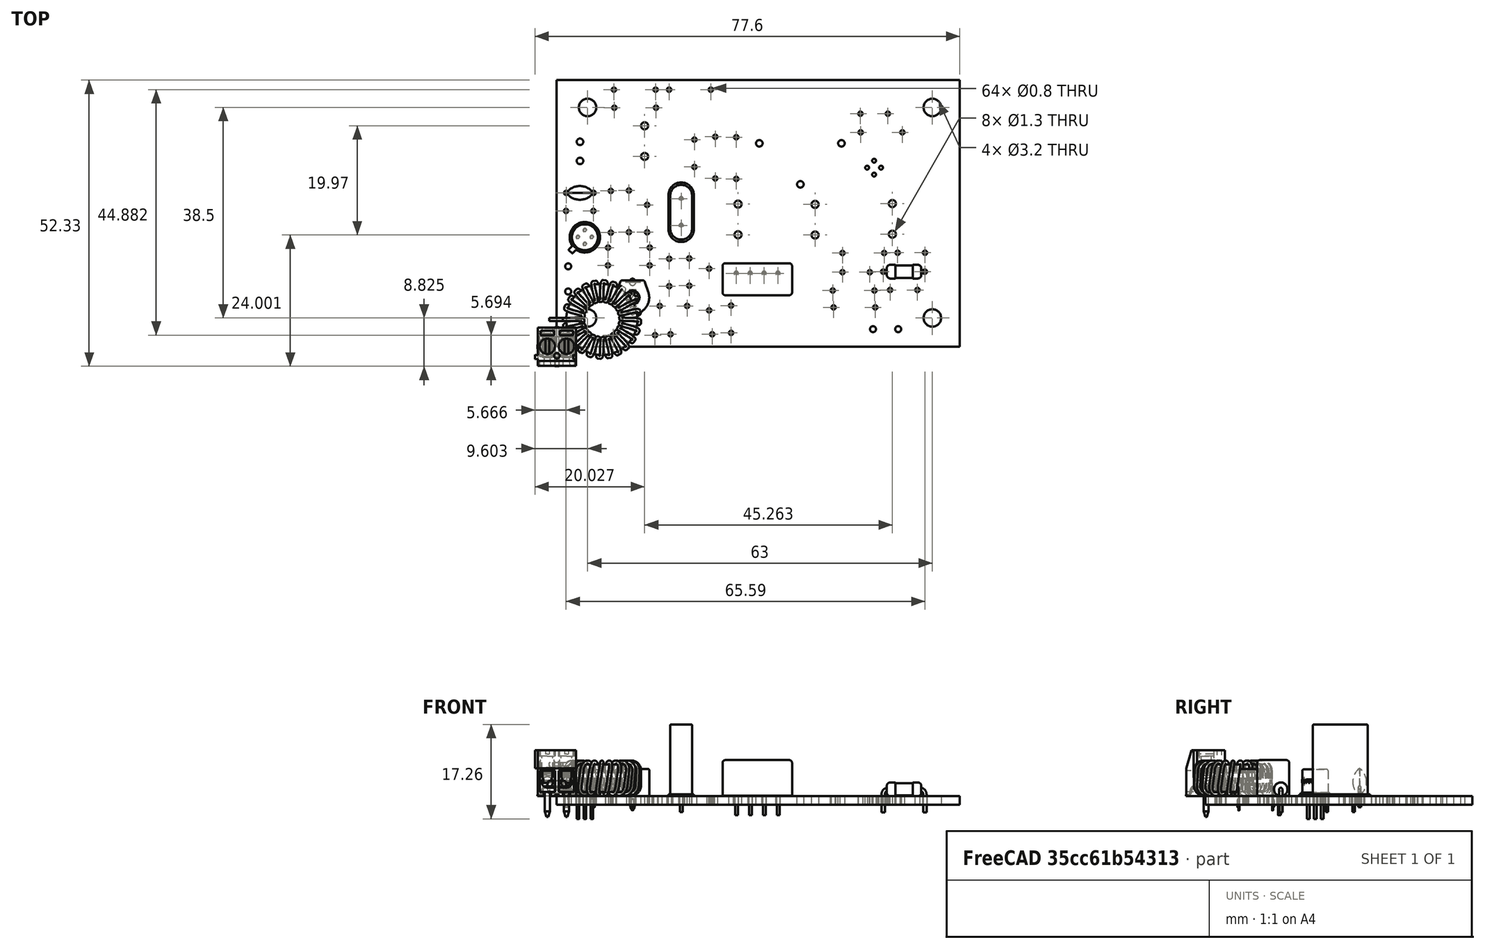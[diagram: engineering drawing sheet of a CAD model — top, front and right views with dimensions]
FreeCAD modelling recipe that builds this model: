
FCSTD DOCUMENT  (FreeCAD 0.19R24267 +148 (Git))
Label: 2ndmixer-2ndlo
License: All rights reserved
LicenseURL: http://en.wikipedia.org/wiki/All_rights_reserved
objects: App::Link×41, Part::Feature×33, App::Part×8, PartDesign::CoordinateSystem×1, Sketcher::SketchObject×1
note: 35 computed .brp shape members not serialized (recipe doc carries the construction recipe); baked Part::Feature solids carry a one-line shape summary decoded from their .brp

FEATURE [PartDesign::CoordinateSystem] Local_CS_b4da
  AttacherType = Attacher::AttachEngine3D
FEATURE [Part::Feature] Pcb_b4da
  Placement = pos=(-101.397,124.765,0) rot=(0,0,1;0rad)
  shape: bbox 73.68 x 48.77 x 1.6 mm, 101 faces (baked)
FEATURE [Sketcher::SketchObject] PCB_Sketch_b4da
  FullyConstrained = false
  sketch-geometry (4):
    g0: LineSegment StartX=-0.077005 StartY=0 StartZ=0 EndX=73.6032 EndY=0 EndZ=0
    g1: LineSegment StartX=73.6032 StartY=48.768 StartZ=0 EndX=-0.077005 EndY=48.768 EndZ=0
    g2: LineSegment StartX=73.6032 StartY=0 StartZ=0 EndX=73.6032 EndY=48.768 EndZ=0
    g3: LineSegment StartX=-0.077005 StartY=48.768 StartZ=0 EndX=-0.077005 EndY=0 EndZ=0
  constraints (4):
    c: Coincident(g0,g3)
    c: Coincident(g1,g3)
    c: Coincident(g0,g2)
    c: Coincident(g1,g2)
FEATURE [Part::Feature] Shape  label="R217_R_Axial_DIN0207_L63mm_D25mm_P762mm_Horizontal_89c8d03f2e72"
  Placement = pos=(59.6138,13.7414,0) rot=(0,0,1;0rad)
  shape: bbox 8.418 x 2.706 x 5.603 mm, 15 faces (baked)
FEATURE [Part::Feature] Shape001  label="C203_C_Disc_D50mm_W25mm_P500mm_089fd93012b2"
  Placement = pos=(6.691,28.1432,0) rot=(0,0,1;3.14159rad)
  shape: bbox 5.5 x 2.5 x 7.1 mm, 10 faces (baked)
FEATURE [App::Link] R217_R_Axial_DIN0207_L63mm_D25mm_P762mm_Horizontal_89c8d03f2e72_ln_  label="R213_R_Axial_DIN0207_L63mm_D25mm_P762mm_Horizontal_cce2eee8a25c"
  LinkPlacement = pos=(55.499,39.2176,0) rot=(0,0,1;0rad)
  LinkedObject = -> Shape
  Placement = pos=(55.499,39.2176,0) rot=(0,0,1;0rad)
FEATURE [App::Link] C203_C_Disc_D50mm_W25mm_P500mm_089fd93012b2_ln_  label="C205_C_Disc_D50mm_W25mm_P500mm_a9d93c2b414c"
  LinkPlacement = pos=(20.5232,16.089,0) rot=(0,0,-1;1.5708rad)
  LinkedObject = -> Shape001
  Placement = pos=(20.5232,16.089,0) rot=(0,0,-1;1.5708rad)
FEATURE [Part::Feature] Shape002  label="C206_Trimmer Cap - Brown_62b893ec28ea"
  Placement = pos=(13.8176,9.011,0) rot=(0,0,1;3.14159rad)
  shape: bbox 6.618 x 6.858 x 7.625 mm, 264 faces (baked)
FEATURE [App::Link] C206_Trimmer_Cap___Brown_62b893ec28ea_ln_  label="C206_Trimmer Cap - Brown_62b893ec28ea[2]"
  LinkPlacement = pos=(13.8176,11.811,0) rot=(0,0,-1;1.5708rad)
  LinkedObject = -> Shape002
  Placement = pos=(13.8176,11.811,0) rot=(0,0,-1;1.5708rad)
FEATURE [App::Link] R217_R_Axial_DIN0207_L63mm_D25mm_P762mm_Horizontal_89c8d03f2e72_ln_001  label="R211_R_Axial_DIN0207_L63mm_D25mm_P762mm_Horizontal_9d0fcc912394"
  LinkPlacement = pos=(32.766,38.3286,0) rot=(0,0,-1;1.5708rad)
  LinkedObject = -> Shape
  Placement = pos=(32.766,38.3286,0) rot=(0,0,-1;1.5708rad)
FEATURE [App::Link] R217_R_Axial_DIN0207_L63mm_D25mm_P762mm_Horizontal_89c8d03f2e72_ln_002  label="R216_R_Axial_DIN0207_L63mm_D25mm_P762mm_Horizontal_da9762c644fc"
  LinkPlacement = pos=(58.166,7.2136,0) rot=(0,0,1;3.14159rad)
  LinkedObject = -> Shape
  Placement = pos=(58.166,7.2136,0) rot=(0,0,1;3.14159rad)
FEATURE [Part::Feature] Part__Feature  label="SOLID"
  Placement = pos=(0,0,4.2) rot=(0,0,1;0rad)
  shape: bbox 8 x 7 x 8.4 mm, 72 faces (baked)
FEATURE [Part::Feature] Part__Feature001  label="SOLID001"
  Placement = pos=(0,0,4.2) rot=(0,0,1;0rad)
  shape: bbox 2.75 x 3.75 x 8.15 mm, 17 faces (baked)
FEATURE [Part::Feature] Part__Feature002  label="SOLID002"
  Placement = pos=(0,0,4.2) rot=(0,0,1;0rad)
  shape: bbox 2.75 x 3.75 x 8.15 mm, 17 faces (baked)
FEATURE [Part::Feature] Part__Feature003  label="SOLID003"
  Placement = pos=(0,0,4.2) rot=(0,0,1;0rad)
  shape: bbox 2.9 x 4.5 x 2.65 mm, 46 faces (baked)
FEATURE [Part::Feature] Part__Feature004  label="SOLID004"
  Placement = pos=(0,0,4.2) rot=(0,0,1;0rad)
  shape: bbox 2.9 x 4.5 x 2.65 mm, 46 faces (baked)
FEATURE [Part::Feature] Part__Feature005  label="SOLID005"
  Placement = pos=(0,0,4.2) rot=(0,0,1;0rad)
  shape: bbox 3.139 x 3.139 x 4.6 mm, 17 faces (baked)
FEATURE [Part::Feature] Part__Feature006  label="SOLID006"
  Placement = pos=(0,0,4.2) rot=(0,0,1;0rad)
  shape: bbox 3.139 x 3.139 x 4.6 mm, 17 faces (baked)
FEATURE [App::Part] _91103110002_1  label="J202_691103110002_1_e432b8dc621c"
  Group = -> [Part__Feature,Part__Feature001,Part__Feature002,Part__Feature003,Part__Feature004,Part__Feature005,Part__Feature006]
  Origin = -> Origin008
  Placement = pos=(4.2164,35.7378,0) rot=(0,0,1;1.5708rad)
FEATURE [App::Link] J202_691103110002_1_e432b8dc621c_ln_  label="J202_691103110002_1_e432b8dc621c[2]"
  LinkPlacement = pos=(4.2164,35.7378,0) rot=(0,0,1;1.5708rad)
  LinkedObject = -> _91103110002_1
  Placement = pos=(4.2164,35.7378,0) rot=(0,0,1;1.5708rad)
FEATURE [App::Link] R217_R_Axial_DIN0207_L63mm_D25mm_P762mm_Horizontal_89c8d03f2e72_ln_003  label="R206_R_Axial_DIN0207_L63mm_D25mm_P762mm_Horizontal_b9c1ee328a49"
  LinkPlacement = pos=(17.9324,2.1336,0) rot=(0,0,1;3.14159rad)
  LinkedObject = -> Shape
  Placement = pos=(17.9324,2.1336,0) rot=(0,0,1;3.14159rad)
FEATURE [App::Link] C203_C_Disc_D50mm_W25mm_P500mm_089fd93012b2_ln_001  label="C212_C_Disc_D50mm_W25mm_P500mm_bde68aed2039"
  LinkPlacement = pos=(62.2554,17.1958,0) rot=(0,0,1;0rad)
  LinkedObject = -> Shape001
  Placement = pos=(62.2554,17.1958,0) rot=(0,0,1;0rad)
FEATURE [App::Link] C203_C_Disc_D50mm_W25mm_P500mm_089fd93012b2_ln_002  label="C209_C_Disc_D50mm_W25mm_P500mm_380680a835a4"
  LinkPlacement = pos=(31.8262,2.54,0) rot=(0,0,1;1.5708rad)
  LinkedObject = -> Shape001
  Placement = pos=(31.8262,2.54,0) rot=(0,0,1;1.5708rad)
FEATURE [App::Link] R217_R_Axial_DIN0207_L63mm_D25mm_P762mm_Horizontal_89c8d03f2e72_ln_004  label="R205_R_Axial_DIN0207_L63mm_D25mm_P762mm_Horizontal_e8206ead489c"
  LinkPlacement = pos=(9.3218,14.8844,0) rot=(0,0,1;0rad)
  LinkedObject = -> Shape
  Placement = pos=(9.3218,14.8844,0) rot=(0,0,1;0rad)
FEATURE [App::Link] R217_R_Axial_DIN0207_L63mm_D25mm_P762mm_Horizontal_89c8d03f2e72_ln_005  label="R203_R_Axial_DIN0207_L63mm_D25mm_P762mm_Horizontal_4a083b21630a"
  LinkPlacement = pos=(13.1572,28.575,0) rot=(0,0,-1;1.5708rad)
  LinkedObject = -> Shape
  Placement = pos=(13.1572,28.575,0) rot=(0,0,-1;1.5708rad)
FEATURE [App::Link] R217_R_Axial_DIN0207_L63mm_D25mm_P762mm_Horizontal_89c8d03f2e72_ln_006  label="R214_R_Axial_DIN0207_L63mm_D25mm_P762mm_Horizontal_72fafbfdd86e"
  LinkPlacement = pos=(58.0136,10.287,0) rot=(0,0,1;3.14159rad)
  LinkedObject = -> Shape
  Placement = pos=(58.0136,10.287,0) rot=(0,0,1;3.14159rad)
FEATURE [App::Link] R217_R_Axial_DIN0207_L63mm_D25mm_P762mm_Horizontal_89c8d03f2e72_ln_007  label="R215_R_Axial_DIN0207_L63mm_D25mm_P762mm_Horizontal_28d317cf12d8"
  LinkPlacement = pos=(20.4978,47.0154,0) rot=(0,0,1;0rad)
  LinkedObject = -> Shape
  Placement = pos=(20.4978,47.0154,0) rot=(0,0,1;0rad)
FEATURE [App::Link] R217_R_Axial_DIN0207_L63mm_D25mm_P762mm_Horizontal_89c8d03f2e72_ln_008  label="R207_R_Axial_DIN0207_L63mm_D25mm_P762mm_Horizontal_df0c2504f956"
  LinkPlacement = pos=(28.3718,2.286,0) rot=(0,0,1;3.14159rad)
  LinkedObject = -> Shape
  Placement = pos=(28.3718,2.286,0) rot=(0,0,1;3.14159rad)
FEATURE [Part::Feature] Part__Feature007  label="part"
  shape: bbox 0.1473 x 0.1473 x 0.003 mm, 3 faces (baked)
FEATURE [Part::Feature] Part__Feature008  label="part001"
  shape: bbox 3.686 x 3.686 x 2.289 mm, 14 faces (baked)
FEATURE [Part::Feature] Part__Feature009  label="part002"
  shape: bbox 1.717 x 0.764 x 1.78 mm, 14 faces (baked)
FEATURE [Part::Feature] Part__Feature010  label="part003"
  shape: bbox 0.764 x 1.717 x 1.78 mm, 14 faces (baked)
FEATURE [Part::Feature] Part__Feature011  label="part004"
  shape: bbox 1.717 x 0.764 x 1.78 mm, 14 faces (baked)
FEATURE [Part::Feature] Part__Feature012  label="part005"
  shape: bbox 0.764 x 1.717 x 1.78 mm, 14 faces (baked)
FEATURE [App::Part] part  label="U201_part006_e06496575535"
  Group = -> [Part__Feature007,Part__Feature008,Part__Feature009,Part__Feature010,Part__Feature011,Part__Feature012]
  Origin = -> Origin009
  Placement = pos=(41.0337,4.8133,0) rot=(0,0,1;0rad)
FEATURE [Part::Feature] Part__Feature013  label="T37-6 IND"
  Placement = pos=(0,-2.7,-0.5) rot=(1,0,0;1.5708rad)
  shape: bbox 10.32 x 3.252 x 10.32 mm, 8 faces, 0 solids (baked)
FEATURE [Part::Feature] Part__Feature014  label="T37-6 IND001"
  Placement = pos=(0,-2.7,-0.5) rot=(1,0,0;1.5708rad)
  shape: bbox 10.51 x 3.773 x 9.618 mm, 81 faces, 0 solids (baked)
FEATURE [Part::Feature] Part__Feature015  label="T37-6 IND002"
  Placement = pos=(0,-2.7,-0.5) rot=(1,0,0;1.5708rad)
  shape: bbox 2.23 x 4.584 x 1.894 mm, 1 faces, 0 solids (baked)
FEATURE [Part::Feature] Part__Feature016  label="T37-6 IND003"
  Placement = pos=(0,-2.7,-0.5) rot=(1,0,0;1.5708rad)
  shape: bbox 1.873 x 4.219 x 1.831 mm, 1 faces, 0 solids (baked)
FEATURE [App::Part] T37_6_IND004  label="L202_T37-6 IND004_038137819fb8"
  Group = -> [Part__Feature013,Part__Feature014,Part__Feature015,Part__Feature016]
  Origin = -> Origin010
  Placement = pos=(61.2902,26.1874,0) rot=(0,0,1;0rad)
FEATURE [App::Link] L202_T37_6_IND004_038137819fb8_ln_  label="L202_T37-6 IND004_038137819fb8[2]"
  LinkPlacement = pos=(61.2902,26.1874,0) rot=(0,0,1;0rad)
  LinkedObject = -> T37_6_IND004
  Placement = pos=(61.2902,26.1874,0) rot=(0,0,1;0rad)
FEATURE [App::Link] R217_R_Axial_DIN0207_L63mm_D25mm_P762mm_Horizontal_89c8d03f2e72_ln_009  label="R201_R_Axial_DIN0207_L63mm_D25mm_P762mm_Horizontal_8da1f1e041d0"
  LinkPlacement = pos=(9.8552,28.4988,0) rot=(0,0,-1;1.5708rad)
  LinkedObject = -> Shape
  Placement = pos=(9.8552,28.4988,0) rot=(0,0,-1;1.5708rad)
FEATURE [App::Link] C203_C_Disc_D50mm_W25mm_P500mm_089fd93012b2_ln_003  label="C208_C_Disc_D50mm_W25mm_P500mm_939057481a42"
  LinkPlacement = pos=(23.7852,7.4676,0) rot=(0,0,1;3.14159rad)
  LinkedObject = -> Shape001
  Placement = pos=(23.7852,7.4676,0) rot=(0,0,1;3.14159rad)
FEATURE [App::Link] C203_C_Disc_D50mm_W25mm_P500mm_089fd93012b2_ln_004  label="C201_C_Disc_D50mm_W25mm_P500mm_a150a43b3eb5"
  LinkPlacement = pos=(6.6656,24.8412,0) rot=(0,0,1;3.14159rad)
  LinkedObject = -> Shape001
  Placement = pos=(6.6656,24.8412,0) rot=(0,0,1;3.14159rad)
FEATURE [Part::Feature] Shape003  label="U202_Body002_17581df04f6c"
  Placement = pos=(32.766,13.4336,0) rot=(0,0,1;0rad)
  shape: bbox 12.7 x 5.84 x 10.04 mm, 26 faces (baked)
FEATURE [App::Link] U202_Body002_17581df04f6c_ln_  label="U202_Body002_17581df04f6c[2]"
  LinkPlacement = pos=(32.766,13.4336,0) rot=(0,0,1;0rad)
  LinkedObject = -> Shape003
  Placement = pos=(32.766,13.4336,0) rot=(0,0,1;0rad)
FEATURE [Part::Feature] Shape004  label="Q201_2N3331_31b1c5c0a01c"
  Placement = pos=(5.1108,20.0299,0) rot=(0,0,1;1.5708rad)
  shape: bbox 9.871 x 5.726 x 9.026 mm, 166 faces (baked)
FEATURE [App::Link] Q201_2N3331_31b1c5c0a01c_ln_  label="Q201_2N3331_31b1c5c0a01c[2]"
  LinkPlacement = pos=(5.1108,20.0299,0) rot=(0,0,1;1.5708rad)
  LinkedObject = -> Shape004
  Placement = pos=(5.1108,20.0299,0) rot=(0,0,1;1.5708rad)
FEATURE [App::Link] R217_R_Axial_DIN0207_L63mm_D25mm_P762mm_Horizontal_89c8d03f2e72_ln_010  label="R208_R_Axial_DIN0207_L63mm_D25mm_P762mm_Horizontal_da094b9ea651"
  LinkPlacement = pos=(27.813,6.6548,0) rot=(0,0,1;1.5708rad)
  LinkedObject = -> Shape
  Placement = pos=(27.813,6.6548,0) rot=(0,0,1;1.5708rad)
FEATURE [App::Link] C203_C_Disc_D50mm_W25mm_P500mm_089fd93012b2_ln_005  label="C207_C_Disc_D50mm_W25mm_P500mm_b71f5eab2dcd"
  LinkPlacement = pos=(24.1808,16.1652,0) rot=(0,0,-1;1.5708rad)
  LinkedObject = -> Shape001
  Placement = pos=(24.1808,16.1652,0) rot=(0,0,-1;1.5708rad)
FEATURE [App::Link] C203_C_Disc_D50mm_W25mm_P500mm_089fd93012b2_ln_006  label="C214_C_Disc_D50mm_W25mm_P500mm_07d36dee86ff"
  LinkPlacement = pos=(65.873,10.3886,0) rot=(0,0,1;3.14159rad)
  LinkedObject = -> Shape001
  Placement = pos=(65.873,10.3886,0) rot=(0,0,1;3.14159rad)
FEATURE [App::Link] C203_C_Disc_D50mm_W25mm_P500mm_089fd93012b2_ln_007  label="C213_C_Disc_D50mm_W25mm_P500mm_87d95f91cfc0"
  LinkPlacement = pos=(60.4628,42.6212,0) rot=(0,0,1;3.14159rad)
  LinkedObject = -> Shape001
  Placement = pos=(60.4628,42.6212,0) rot=(0,0,1;3.14159rad)
FEATURE [App::Link] R217_R_Axial_DIN0207_L63mm_D25mm_P762mm_Horizontal_89c8d03f2e72_ln_011  label="R202_R_Axial_DIN0207_L63mm_D25mm_P762mm_Horizontal_28998dc9bd10"
  LinkPlacement = pos=(9.3472,18.1356,0) rot=(0,0,1;0rad)
  LinkedObject = -> Shape
  Placement = pos=(9.3472,18.1356,0) rot=(0,0,1;0rad)
FEATURE [App::Link] R217_R_Axial_DIN0207_L63mm_D25mm_P762mm_Horizontal_89c8d03f2e72_ln_012  label="R210_R_Axial_DIN0207_L63mm_D25mm_P762mm_Horizontal_304976f6f522"
  LinkPlacement = pos=(10.414,47.0154,0) rot=(0,0,1;0rad)
  LinkedObject = -> Shape
  Placement = pos=(10.414,47.0154,0) rot=(0,0,1;0rad)
FEATURE [App::Link] C203_C_Disc_D50mm_W25mm_P500mm_089fd93012b2_ln_008  label="C211_C_Disc_D50mm_W25mm_P500mm_938715400f50"
  LinkPlacement = pos=(57.1754,13.6398,0) rot=(0,0,1;3.14159rad)
  LinkedObject = -> Shape001
  Placement = pos=(57.1754,13.6398,0) rot=(0,0,1;3.14159rad)
FEATURE [App::Link] R217_R_Axial_DIN0207_L63mm_D25mm_P762mm_Horizontal_89c8d03f2e72_ln_013  label="R212_R_Axial_DIN0207_L63mm_D25mm_P762mm_Horizontal_e728fa45b572"
  LinkPlacement = pos=(52.1716,17.145,0) rot=(0,0,1;0rad)
  LinkedObject = -> Shape
  Placement = pos=(52.1716,17.145,0) rot=(0,0,1;0rad)
FEATURE [Part::Feature] Shape005  label="Y201_Crystal_HC49-U_Vertical_7b5f2de54ed7"
  Placement = pos=(22.7076,27.051,0) rot=(0,0,-1;1.5708rad)
  shape: bbox 4.65 x 10.9 x 16 mm, 26 faces (baked)
FEATURE [App::Link] C203_C_Disc_D50mm_W25mm_P500mm_089fd93012b2_ln_009  label="C210_C_Disc_D50mm_W25mm_P500mm_7240768806ec"
  LinkPlacement = pos=(25.1206,37.8822,0) rot=(0,0,-1;1.5708rad)
  LinkedObject = -> Shape001
  Placement = pos=(25.1206,37.8822,0) rot=(0,0,-1;1.5708rad)
FEATURE [App::Link] R217_R_Axial_DIN0207_L63mm_D25mm_P762mm_Horizontal_89c8d03f2e72_ln_014  label="R209_R_Axial_DIN0207_L63mm_D25mm_P762mm_Horizontal_1e766996dd06"
  LinkPlacement = pos=(28.9306,38.4048,0) rot=(0,0,-1;1.5708rad)
  LinkedObject = -> Shape
  Placement = pos=(28.9306,38.4048,0) rot=(0,0,-1;1.5708rad)
FEATURE [App::Link] Q201_2N3331_31b1c5c0a01c_ln_001  label="Q202_2N3331_59fc3119a439"
  LinkPlacement = pos=(57.9521,32.7606,0) rot=(0,0,1;0rad)
  LinkedObject = -> Shape004
  Placement = pos=(57.9521,32.7606,0) rot=(0,0,1;0rad)
FEATURE [App::Link] Q201_2N3331_31b1c5c0a01c_ln_002  label="Q202_2N3331_59fc3119a439[2]"
  LinkPlacement = pos=(57.9521,32.7606,0) rot=(0,0,1;0rad)
  LinkedObject = -> Shape004
  Placement = pos=(57.9521,32.7606,0) rot=(0,0,1;0rad)
FEATURE [App::Link] L202_T37_6_IND004_038137819fb8_ln_001  label="L204_T37-6 IND004_7a62be4f95a9"
  LinkPlacement = pos=(47.1678,26.041,0) rot=(0,0,1;0rad)
  LinkedObject = -> T37_6_IND004
  Placement = pos=(47.1678,26.041,0) rot=(0,0,1;0rad)
FEATURE [App::Link] L202_T37_6_IND004_038137819fb8_ln_002  label="L204_T37-6 IND004_7a62be4f95a9[2]"
  LinkPlacement = pos=(47.1678,26.041,0) rot=(0,0,1;0rad)
  LinkedObject = -> T37_6_IND004
  Placement = pos=(47.1678,26.041,0) rot=(0,0,1;0rad)
FEATURE [App::Link] L202_T37_6_IND004_038137819fb8_ln_003  label="L203_T37-6 IND004_40d8894a6aec"
  LinkPlacement = pos=(33.0962,26.0918,0) rot=(0,0,1;0rad)
  LinkedObject = -> T37_6_IND004
  Placement = pos=(33.0962,26.0918,0) rot=(0,0,1;0rad)
FEATURE [App::Link] L202_T37_6_IND004_038137819fb8_ln_004  label="L203_T37-6 IND004_40d8894a6aec[2]"
  LinkPlacement = pos=(33.0962,26.0918,0) rot=(0,0,1;0rad)
  LinkedObject = -> T37_6_IND004
  Placement = pos=(33.0962,26.0918,0) rot=(0,0,1;0rad)
FEATURE [Part::Feature] Part__Feature017  label="L_Tor_13x8x5_3a_cp"
  shape: bbox 14.07 x 14.07 x 5 mm, 8 faces (baked)
FEATURE [Part::Feature] Part__Feature018  label="L_Tor_13x8x5_3a_cp001"
  shape: bbox 16.93 x 14.67 x 6.694 mm, 203 faces (baked)
FEATURE [App::Part] L_Tor_13x8x5_3a_cp  label="T201_L_Tor_13x8x5_3a_cp002_c358b2f006f9"
  Group = -> [Part__Feature017,Part__Feature018]
  Origin = -> Origin011
  Placement = pos=(36.9824,32.211,0) rot=(0,0,1;0rad)
FEATURE [App::Link] T201_L_Tor_13x8x5_3a_cp002_c358b2f006f9_ln_  label="T201_L_Tor_13x8x5_3a_cp002_c358b2f006f9[2]"
  LinkPlacement = pos=(36.9824,32.211,0) rot=(0,0,1;0rad)
  LinkedObject = -> L_Tor_13x8x5_3a_cp
  Placement = pos=(36.9824,32.211,0) rot=(0,0,1;0rad)
FEATURE [App::Link] R217_R_Axial_DIN0207_L63mm_D25mm_P762mm_Horizontal_89c8d03f2e72_ln_015  label="R204_R_Axial_DIN0207_L63mm_D25mm_P762mm_Horizontal_7511eed1eca9"
  LinkPlacement = pos=(10.4902,43.7134,0) rot=(0,0,1;0rad)
  LinkedObject = -> Shape
  Placement = pos=(10.4902,43.7134,0) rot=(0,0,1;0rad)
FEATURE [App::Link] C203_C_Disc_D50mm_W25mm_P500mm_089fd93012b2_ln_010  label="C204_C_Disc_D50mm_W25mm_P500mm_bd8674b6b8b7"
  LinkPlacement = pos=(16.4846,25.9442,0) rot=(0,0,-1;1.5708rad)
  LinkedObject = -> Shape001
  Placement = pos=(16.4846,25.9442,0) rot=(0,0,-1;1.5708rad)
FEATURE [App::Link] L202_T37_6_IND004_038137819fb8_ln_005  label="L201_T37-6 IND004_bc16f2046b3e"
  LinkPlacement = pos=(16.0274,40.4114,0) rot=(0,0,1;0rad)
  LinkedObject = -> T37_6_IND004
  Placement = pos=(16.0274,40.4114,0) rot=(0,0,1;0rad)
FEATURE [App::Link] L202_T37_6_IND004_038137819fb8_ln_006  label="L201_T37-6 IND004_bc16f2046b3e[2]"
  LinkPlacement = pos=(16.0274,40.4114,0) rot=(0,0,1;0rad)
  LinkedObject = -> T37_6_IND004
  Placement = pos=(16.0274,40.4114,0) rot=(0,0,1;0rad)
FEATURE [App::Part] Top_b4da
  Group = -> [Shape,Shape001,R217_R_Axial_DIN0207_L63mm_D25mm_P762mm_Horizontal_89c8d03f2e72_ln_,C203_C_Disc_D50mm_W25mm_P500mm_089fd93012b2_ln_,Shape002,C206_Trimmer_Cap___Brown_62b893ec28ea_ln_,R217_R_Axial_DIN0207_L63mm_D25mm_P762mm_Horizontal_89c8d03f2e72_ln_001,R217_R_Axial_DIN0207_L63mm_D25mm_P762mm_Horizontal_89c8d03f2e72_ln_002,_91103110002_1,J202_691103110002_1_e432b8dc621c_ln_,+41 more]
  Origin = -> Origin003
FEATURE [App::Part] Step_Models_b4da
  Group = -> [Top_b4da]
  Origin = -> Origin002
FEATURE [Part::Feature] pads_area057001  label="topPads_b4da"
  Placement = pos=(-101.397,124.765,0.02) rot=(0,0,1;0rad)
  shape: bbox 67.19 x 46.92 x 2e-07 mm, 105 faces, 0 solids (baked)
FEATURE [Part::Feature] Shape006001  label="topTracks_b4da"
  Placement = pos=(-101.397,124.765,0.01) rot=(0,0,1;0rad)
  shape: bbox 65.81 x 47.03 x 2e-07 mm, 34 faces, 0 solids (baked)
FEATURE [Part::Feature] zones_area001  label="topZones_b4da"
  Placement = pos=(-101.397,124.765,0.01) rot=(0,0,1;0rad)
  shape: bbox 72.92 x 48.01 x 2e-07 mm, 7 faces, 0 solids (baked)
FEATURE [Part::Feature] pads_area057048001  label="botPads_b4da"
  Placement = pos=(-101.397,124.765,-1.62) rot=(0,0,1;0rad)
  shape: bbox 67.19 x 46.48 x 2e-07 mm, 91 faces, 0 solids (baked)
FEATURE [Part::Feature] Shape006002001  label="botTracks_b4da"
  Placement = pos=(-101.397,124.765,-1.61) rot=(0,0,1;0rad)
  shape: bbox 61.46 x 44.32 x 2e-07 mm, 29 faces, 0 solids (baked)
FEATURE [Part::Feature] zones_area002001  label="botZones_b4da"
  Placement = pos=(-101.397,124.765,-1.61) rot=(0,0,1;0rad)
  shape: bbox 72.92 x 48.01 x 2e-07 mm, 2 faces, 0 solids (baked)
FEATURE [Part::Feature] topSilks_2fb8
  Placement = pos=(-101.397,124.765,0.07) rot=(0,0,1;0rad)
  shape: bbox 71.94 x 48.22 x 2e-07 mm, 467 faces, 0 solids (baked)
FEATURE [App::Part] Board_Geoms_b4da
  Group = -> [Local_CS_b4da,Pcb_b4da,PCB_Sketch_b4da,pads_area057001,Shape006001,zones_area001,pads_area057048001,Shape006002001,zones_area002001,topSilks_2fb8]
  Origin = -> Origin
FEATURE [App::Part] Board_b4da  label="2ndmixer-2ndlo"
  Group = -> [Board_Geoms_b4da,Step_Models_b4da]
  Origin = -> Origin001
